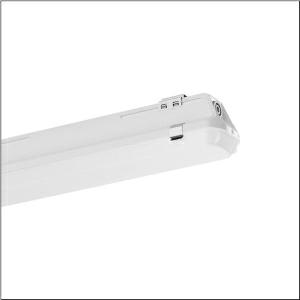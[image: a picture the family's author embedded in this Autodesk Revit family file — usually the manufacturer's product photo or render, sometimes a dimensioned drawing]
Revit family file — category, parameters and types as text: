
# Revit family: monsun_r__11_51fp10dp460h_8c07
name_source: partatom
category: Lighting Fixtures
units: mm (PartAtom-declared; Revit-internal decimal feet)

## family parameters
Cut with Voids When Loaded = No
Host = Face
Light Source = No
Part Type = Normal
Room Calculation Point = No
Round Connector Dimension = Use Diameter
Shared = No

## types (1)
- --- (1 x LED, 6050 lm, 34.6 W, 4000K)
    Apparent Load = 35 VA
    CIE Flux Codes = 47 77 93 94 100
    Color Rendering = 80
    Color Temperature = 4000K
    Default Elevation = 1800 mm
    Description = Monsun® 11, damp-proof luminaire, chain hanger, primary optical cover: enclosure, of PMMA, light emission: direct distribution, primary light characteristic: symmetric, installation type: suspended mounting, surface-mounted, horizontal mounting, vertical mounting, LED, rated luminous flux: 6.050lm, luminous efficacy: 175lm/W, light colour: 840, colour temperature: 4000K, control gear: ECG DALI, with terminal, 5-pole, max. 2.5mm², mains connection: 220..240V, AC, 50/60Hz, rated input power: 35W, luminaire housing, of glass-fibre reinforced polyester, uncoated, bright grey, incl. chain hanger, length: 1.590mm, width: 90mm, height: 88mm, clip for enclosure, of stainless steel (V2A), ceiling mounting element, of stainless steel (V2A), chain hanger, of stainless steel (V2A), protection rating (complete): IP66, insulation class (complete): insulation class I (protective earthing), certification: CE, ENEC, VDE, UKCA, protection symbol: D, impact resistance: IK04, permissible operating ambient temperature: -25..+40°C, standard: EN 50419, EN 60598-2-1, no direct snow, no direct sun, no direct rain, for indoor or canopied outdoor use, corresponds to IFS (International Featured Standards) requirements for safety and quality in the food industry, contact your sales advisor before using the luminaires in applications with unclear chemical exposure, large temperature fluctuations or condensation-forming humidity, LABS conformity tested according to VDMA 24364:2018-05, packaging unit: 1 piece
    Height = 89 mm
    Lamp = 1 x LED
    Lamp Light Flux = 6050 lm
    Lamp Power = 34.6 W
    Lamp count = 1
    Length = 1590 mm
    Luminous efficacy = 175 lm/W
    Manufacturer = Siteco
    ModVariant = No
    Model = 51FP10DP460H
    Mounting Place = Ceiling
    Mounting Type = Surface mounted
    Number of Poles = 1
    OnlyDefault = Yes
    Power Factor = 1
    Product Name = Monsun® 11
    Product group = damp-proof luminaire
    ProductGroupID = 300
    Protection Class = Protection class I
    Protection Degree = IP 66
    RLX_Detail_Level = 1
    RLX_Emergency_Light_Flux = 0 lm
    RLX_Emergency_Type = 0
    RLX_Emergency_Type_DB = No
    RlxData = <blob elided: 92281 chars, md5=b949ff08>
    Socket = socket
    Standby Power = 0 W
    System Light Flux = 6050 lm
    System Power = 35 W
    Type Comments = factory setting: luminous flux: 100 % | dim-lin: 254 | 232 mA
    Type Image = l_1319650.jpg
    URL = http://relux.com
    VarID = @adj_174731
    Voltage = 0 V
    Weight = 0.00 kg
    Width = 90 mm

## geometry (parser evidence)
native form markers: Blend x4, Sweep x15
no freeform markers — native parametric forms only
